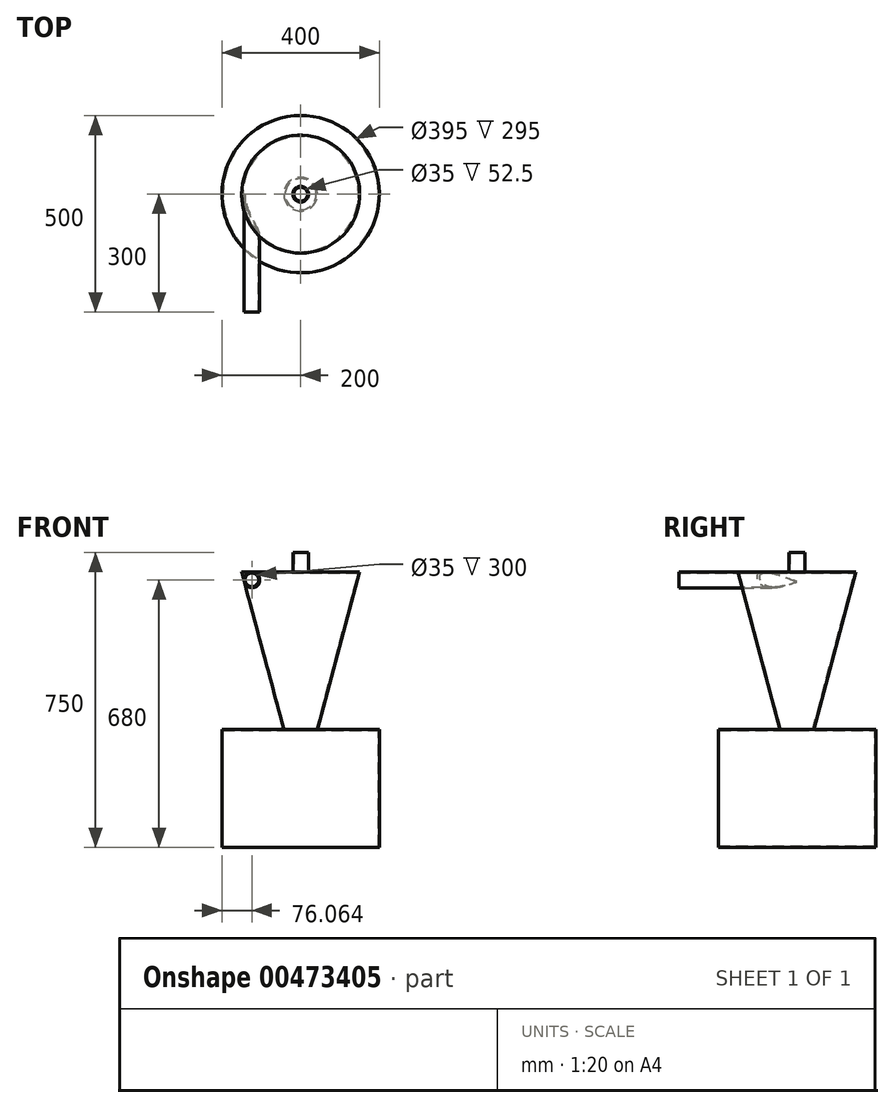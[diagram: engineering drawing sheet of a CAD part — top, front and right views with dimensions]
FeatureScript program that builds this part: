
annotation { "Feature Type Name" : "Feature", "Feature Type Description" : "" }
export const myFeature = defineFeature(function(context is Context, id is Id, definition is map)
    precondition{}
    {
        {
            var Q0;
            Q0=qCreatedBy(makeId("Top.planeOp"),FACE);
            var sketch = newSketch(context, id + "F0", { "sketchPlane" : qUnion([Q0])});
            skCircle(sketch, "E0", {"center": v(0, 0) * mm, "radius": 150 * mm});
            skSolve(sketch);
        }
        {
            var Q0;
            Q0=makeQuery(id+"F0.imprint","IMPRINT",FACE,{"disambiguationData":[TD([[makeQuery(id+"F0.imprint","IMPRINT",EDGE,{"derivedFrom":sQuery(id+"F0.wireOp",EDGE,"E0")}),1.0]])]});
            extrude(context, id + "F1", {"entities" : qUnion([Q0]), "oppositeDirection" : true, "depth" : 400 * mm, "hasDraft" : true, "draftAngle" : 15 * degree, "draftPullDirection" : true});
        }
        {
            var Q0;
            Q0=qCreatedBy(makeId("Front.planeOp"),FACE);
            var sketch = newSketch(context, id + "F2", { "sketchPlane" : qUnion([Q0])});
            skCircle(sketch, "E1", {"center": v(-123.94, -20) * mm, "radius": 20 * mm});
            skLineSegment(sketch, "E2", {"start": v(-42.82, -400) * mm, "end": v(-150, 0) * mm});
            skSolve(sketch);
        }
        {
            var Q0;
            Q0 = qSketchRegion(id + "F2", true);
            extrude(context, id + "F3", {"entities" : qUnion([Q0]), "operationType" : NewBodyOperationType.ADD, "depth" : 300 * mm});
        }
        {
            var Q0;
            Q0=makeQuery(id+"F1.opExtrude","CAP_FACE",FACE,{"disambiguationData":[OSD([sQuery(id+"F0.wireOp",EDGE,"E0")])],"isStart":false});
            var sketch = newSketch(context, id + "F4", { "sketchPlane" : qUnion([Q0])});
            skCircle(sketch, "E3", {"center": v(0, 0) * mm, "radius": 200 * mm});
            skSolve(sketch);
        }
        {
            var Q0;
            Q0 = qSketchRegion(id + "F4", true);
            extrude(context, id + "F5", {"entities" : qUnion([Q0]), "operationType" : NewBodyOperationType.ADD, "depth" : 300 * mm});
        }
        {
            var Q0;
            Q0=makeQuery(id+"F1.opExtrude","CAP_FACE",FACE,{"disambiguationData":[OSD([sQuery(id+"F0.wireOp",EDGE,"E0")])],"isStart":true});
            var sketch = newSketch(context, id + "F6", { "sketchPlane" : qUnion([Q0])});
            skCircle(sketch, "E4", {"center": v(0, 0) * mm, "radius": 20 * mm});
            skSolve(sketch);
        }
        {
            var Q0;
            Q0 = qSketchRegion(id + "F6", true);
            var Q1;
            Q1=makeQuery(id+"F6.imprint","IMPRINT",FACE,{"disambiguationData":[TD([[makeQuery(id+"F6.imprint","IMPRINT",EDGE,{"derivedFrom":sQuery(id+"F6.wireOp",EDGE,"E4")}),1.0]])]});
            extrude(context, id + "F7", {"entities" : qUnion([Q0, Q1]), "operationType" : NewBodyOperationType.ADD, "depth" : 50 * mm});
        }
        {
            var Q0;
            Q0=makeQuery(id+"F7.opExtrude","CAP_FACE",FACE,{"disambiguationData":[OSD([sQuery(id+"F6.wireOp",EDGE,"E4")])],"isStart":false});
            var Q1;
            Q1=makeQuery(id+"F3.opExtrude","CAP_FACE",FACE,{"disambiguationData":[OSD([sQuery(id+"F2.wireOp",EDGE,"E1")])],"isStart":false});
            shell(context, id + "F8", {"entities" : qUnion([Q0, Q1]), "thickness" : 2.5 * mm});
        }
    });
